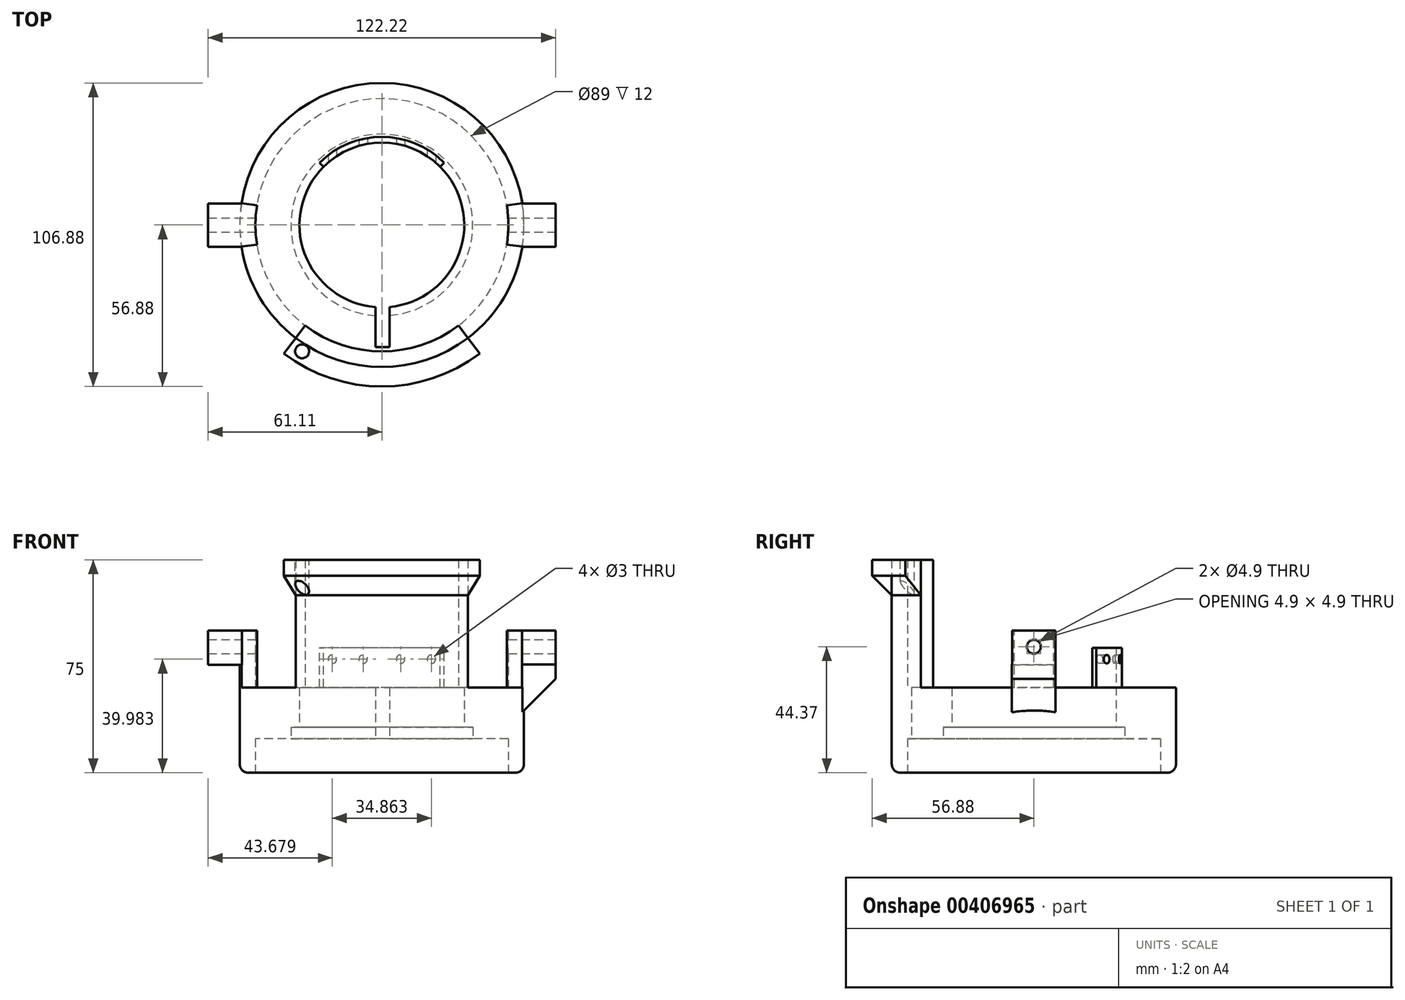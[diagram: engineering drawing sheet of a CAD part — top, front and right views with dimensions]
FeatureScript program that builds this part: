
annotation { "Feature Type Name" : "Feature", "Feature Type Description" : "" }
export const myFeature = defineFeature(function(context is Context, id is Id, definition is map)
    precondition{}
    {
        {
            var Q0;
            Q0=qCreatedBy(makeId("Top.planeOp"),FACE);
            var sketch = newSketch(context, id + "F0", { "sketchPlane" : qUnion([Q0])});
            skCircle(sketch, "E0", {"center": v(0, 0) * mm, "radius": 32 * mm});
            skCircle(sketch, "E1", {"center": v(0, 0) * mm, "radius": 44.5 * mm});
            skCircle(sketch, "E2", {"center": v(0, 0) * mm, "radius": 50 * mm});
            skCircle(sketch, "E3", {"center": v(0, 0) * mm, "radius": 29 * mm});
            skSolve(sketch);
        }
        {
            var Q0;
            Q0=makeQuery(id+"F0.imprint","IMPRINT",FACE,{"disambiguationData":[TD([[makeQuery(id+"F0.imprint","IMPRINT",EDGE,{"derivedFrom":sQuery(id+"F0.wireOp",EDGE,"E1")}),-1.0]])]});
            extrude(context, id + "F1", {"entities" : qUnion([Q0]), "depth" : 50 * mm});
        }
        {
            var Q0;
            Q0=makeQuery(id+"F0.imprint","IMPRINT",FACE,{"disambiguationData":[TD([[makeQuery(id+"F0.imprint","IMPRINT",EDGE,{"derivedFrom":sQuery(id+"F0.wireOp",EDGE,"E0")}),-1.0]])]});
            extrude(context, id + "F2", {"entities" : qUnion([Q0]), "operationType" : NewBodyOperationType.ADD, "depth" : 30 * mm, "hasSecondDirection" : true, "secondDirectionOppositeDirection" : false, "secondDirectionDepth" : 12 * mm});
        }
        {
            var Q0;
            Q0=makeQuery(id+"F0.imprint","IMPRINT",FACE,{"disambiguationData":[TD([[makeQuery(id+"F0.imprint","IMPRINT",EDGE,{"derivedFrom":sQuery(id+"F0.wireOp",EDGE,"E0")}),1.0]])]});
            extrude(context, id + "F3", {"entities" : qUnion([Q0]), "operationType" : NewBodyOperationType.ADD, "depth" : 30 * mm, "hasSecondDirection" : true, "secondDirectionOppositeDirection" : false, "secondDirectionDepth" : 16 * mm});
        }
        {
            var Q0;
            Q0=qCreatedBy(makeId("Top.planeOp"),FACE);
            var sketch = newSketch(context, id + "F4", { "sketchPlane" : qUnion([Q0])});
            skLineSegment(sketch, "E4.bottom", {"start": v(-2.3, -43.05) * mm, "end": v(2.7, -43.05) * mm});
            skLineSegment(sketch, "E4.top", {"start": v(-2.3, -28.05) * mm, "end": v(2.7, -28.05) * mm});
            skLineSegment(sketch, "E4.left", {"start": v(-2.3, -43.05) * mm, "end": v(-2.3, -28.05) * mm});
            skLineSegment(sketch, "E4.right", {"start": v(2.7, -43.05) * mm, "end": v(2.7, -28.05) * mm});
            skSolve(sketch);
        }
        {
            var Q0;
            Q0=makeQuery(id+"F4.imprint","IMPRINT",FACE,{"disambiguationData":[TD([[makeQuery(id+"F4.imprint","IMPRINT",EDGE,{"derivedFrom":sQuery(id+"F4.wireOp",EDGE,"E4.bottom")}),1.0]])]});
            var Q1;
            Q1=sQuery(id+"F4.wireOp",EDGE,"E4.right");
            var Q2;
            Q2=sQuery(id+"F4.wireOp",EDGE,"E4.top");
            var Q3;
            Q3=sQuery(id+"F4.wireOp",EDGE,"E4.left");
            var Q4;
            Q4=sQuery(id+"F4.wireOp",EDGE,"E4.bottom");
            extrude(context, id + "F5", {"entities" : qUnion([Q0]), "operationType" : NewBodyOperationType.REMOVE, "surfaceEntities" : qUnion([Q1, Q2, Q3, Q4]), "depth" : 35 * mm});
        }
        {
            var Q0;
            Q0=makeQuery(id+"F1.opExtrude","CAP_FACE",FACE,{"disambiguationData":[OSD([sQuery(id+"F0.wireOp",EDGE,"E1"),sQuery(id+"F0.wireOp",EDGE,"E2")])],"isStart":false});
            var sketch = newSketch(context, id + "F6", { "sketchPlane" : qUnion([Q0])});
            skLineSegment(sketch, "E5", {"start": v(30.3, -39.78) * mm, "end": v(26.96, -35.4) * mm});
            skLineSegment(sketch, "E6.MirrorCS", {"start": v(-30.3, -39.78) * mm, "end": v(-26.96, -35.4) * mm});
            skSolve(sketch);
        }
        {
            var Q0;
            Q0 = qSketchRegion(id + "F6", true);
            var Q1;
            {var subQ0=sQuery(id+"F6.wireOp",EDGE,"E5");Q1=makeQuery(id+"F6.imprint","IMPRINT",FACE,{"disambiguationData":[TD([[makeQuery(id+"F6.imprint","IMPRINT",EDGE,{"derivedFrom":subQ0}),1.0]])]});}
            extrude(context, id + "F7", {"entities" : qUnion([Q0, Q1]), "operationType" : NewBodyOperationType.ADD, "depth" : 25 * mm});
        }
        {
            var Q0;
            Q0=qCreatedBy(makeId("Right.planeOp"),FACE);
            var sketch = newSketch(context, id + "F8", { "sketchPlane" : qUnion([Q0])});
            skCircle(sketch, "E7", {"center": v(0, 44.37) * mm, "radius": 2.45 * mm});
            skSolve(sketch);
        }
        {
            var Q0;
            Q0=makeQuery(id+"F7.opExtrude","CAP_FACE",FACE,{"disambiguationData":[OSD([sQuery(id+"F0.wireOp",EDGE,"E1"),sQuery(id+"F0.wireOp",EDGE,"E2"),sQuery(id+"F6.wireOp",EDGE,"E5"),sQuery(id+"F6.wireOp",EDGE,"87c34836-5ebc-4285-9b58-168e83040a5a0.MirrorCS")])],"isStart":false});
            var sketch = newSketch(context, id + "F9", { "sketchPlane" : qUnion([Q0])});
            skCircle(sketch, "E8", {"center": v(-28.06, -44.5) * mm, "radius": 2.45 * mm});
            skCircle(sketch, "E9.MirrorC", {"center": v(28.06, -44.5) * mm, "radius": 2.45 * mm});
            skSolve(sketch);
        }
        {
            var Q0;
            Q0=qCreatedBy(makeId("Right.planeOp"),FACE);
            var sketch = newSketch(context, id + "F10", { "sketchPlane" : qUnion([Q0])});
            skLineSegment(sketch, "E10", {"start": v(0, 75.03) * mm, "end": v(0, -13.13) * mm});
            skSolve(sketch);
        }
        {
            var Q0;
            Q0=makeQuery(id+"F7.opExtrude","SWEPT_FACE",FACE,{"disambiguationData":[OSD([sQuery(id+"F6.wireOp",EDGE,"E5")])]});
            var sketch = newSketch(context, id + "F11", { "sketchPlane" : qUnion([Q0])});
            skLineSegment(sketch, "E11", {"start": v(-44.5, 75) * mm, "end": v(-56.88, 75) * mm});
            skLineSegment(sketch, "E12", {"start": v(-50, 62.5) * mm, "end": v(-50, 75) * mm});
            skLineSegment(sketch, "E13", {"start": v(-56.88, 75) * mm, "end": v(-56.88, 69.4) * mm});
            skLineSegment(sketch, "E14", {"start": v(-56.88, 69.4) * mm, "end": v(-50, 62.5) * mm});
            skSolve(sketch);
        }
        {
            var Q0;
            {var subQ0=sQuery(id+"F11.wireOp",EDGE,"E12");Q0=makeQuery(id+"F11.imprint","IMPRINT",FACE,{"disambiguationData":[TD([[makeQuery(id+"F11.imprint","IMPRINT",EDGE,{"derivedFrom":subQ0}),-1.0]])]});}
            var Q1;
            Q1=sQuery(id+"F10.wireOp",EDGE,"E10");
            revolve(context, id + "F12", {"entities" : qUnion([Q0]), "axis" : qUnion([Q1]), "revolveType" : RevolveType.ONE_DIRECTION, "angle" : 74.6 * degree});
        }
        {
            var Q0;
            Q0=makeQuery(id+"F9.imprint","IMPRINT",FACE,{"disambiguationData":[TD([[makeQuery(id+"F9.imprint","IMPRINT",EDGE,{"derivedFrom":sQuery(id+"F9.wireOp",EDGE,"E8")}),1.0]])]});
            var Q1;
            Q1=makeQuery(id+"F9.imprint","IMPRINT",FACE,{"disambiguationData":[TD([[makeQuery(id+"F9.imprint","IMPRINT",EDGE,{"derivedFrom":sQuery(id+"F9.wireOp",EDGE,"E9.MirrorC")}),-1.0]])]});
            extrude(context, id + "F13", {"entities" : qUnion([Q0, Q1]), "operationType" : NewBodyOperationType.REMOVE, "oppositeDirection" : true, "depth" : 25 * mm});
        }
        {
            var Q0;
            Q0=makeQuery(id+"F1.opExtrude","CAP_FACE",FACE,{"disambiguationData":[OSD([sQuery(id+"F0.wireOp",EDGE,"E1"),sQuery(id+"F0.wireOp",EDGE,"E2")])],"isStart":false});
            var sketch = newSketch(context, id + "F14", { "sketchPlane" : qUnion([Q0])});
            skLineSegment(sketch, "E15", {"start": v(49.42, -7.62) * mm, "end": v(43.96, -6.9) * mm});
            skLineSegment(sketch, "E16.MirrorCS", {"start": v(49.42, 7.62) * mm, "end": v(43.96, 6.9) * mm});
            skLineSegment(sketch, "E17.MirrorCS", {"start": v(-49.42, 7.62) * mm, "end": v(-43.96, 6.9) * mm});
            skLineSegment(sketch, "E18.MirrorCS", {"start": v(-49.42, -7.62) * mm, "end": v(-43.96, -6.9) * mm});
            skSolve(sketch);
        }
        {
            var Q0;
            {var subQ0=sQuery(id+"F14.wireOp",EDGE,"E15");Q0=makeQuery(id+"F14.imprint","IMPRINT",FACE,{"disambiguationData":[TD([[makeQuery(id+"F14.imprint","IMPRINT",EDGE,{"derivedFrom":subQ0}),1.0]])]});}
            var Q1;
            {var subQ0=sQuery(id+"F14.wireOp",EDGE,"E16.MirrorCS");Q1=makeQuery(id+"F14.imprint","IMPRINT",FACE,{"disambiguationData":[TD([[makeQuery(id+"F14.imprint","IMPRINT",EDGE,{"derivedFrom":subQ0}),-1.0]])]});}
            var Q2;
            {var subQ0=sQuery(id+"F14.wireOp",EDGE,"E18.MirrorCS");Q2=makeQuery(id+"F14.imprint","IMPRINT",FACE,{"disambiguationData":[TD([[makeQuery(id+"F14.imprint","IMPRINT",EDGE,{"derivedFrom":subQ0}),-1.0]])]});}
            extrude(context, id + "F15", {"entities" : qUnion([Q0, Q1, Q2]), "operationType" : NewBodyOperationType.REMOVE, "oppositeDirection" : true, "depth" : 20 * mm});
        }
        {
            var Q0;
            Q0=qCreatedBy(makeId("Top.planeOp"),FACE);
            var sketch = newSketch(context, id + "F16", { "sketchPlane" : qUnion([Q0])});
            skLineSegment(sketch, "E19.MirrorCS", {"start": v(-61.11, 7.6) * mm, "end": v(-49.36, 7.6) * mm});
            skLineSegment(sketch, "E20.MirrorCS", {"start": v(-49.3, -7.68) * mm, "end": v(-61.11, -7.68) * mm});
            skLineSegment(sketch, "E21.MirrorCS", {"start": v(-61.11, -7.68) * mm, "end": v(-61.11, 7.6) * mm});
            skArc(sketch, "E22", {"start": v(-49.36, 7.6) * mm, "mid": v(-49.86, -0.04) * mm, "end": v(-49.3, -7.68) * mm});
            skLineSegment(sketch, "E23.MirrorCS", {"start": v(61.11, 7.6) * mm, "end": v(49.36, 7.6) * mm});
            skLineSegment(sketch, "E24.MirrorCS", {"start": v(61.11, -7.68) * mm, "end": v(61.11, 7.6) * mm});
            skLineSegment(sketch, "E25.MirrorCS", {"start": v(49.3, -7.68) * mm, "end": v(61.11, -7.68) * mm});
            skArc(sketch, "E26.MirrorCS", {"start": v(49.36, 7.6) * mm, "mid": v(49.86, -0.04) * mm, "end": v(49.3, -7.68) * mm});
            skSolve(sketch);
        }
        {
            var Q0;
            Q0=makeQuery(id+"F16.imprint","IMPRINT",FACE,{"disambiguationData":[TD([[makeQuery(id+"F16.imprint","IMPRINT",EDGE,{"derivedFrom":sQuery(id+"F16.wireOp",EDGE,"E19.MirrorCS")}),-1.0]])]});
            var Q1;
            Q1=makeQuery(id+"F16.imprint","IMPRINT",FACE,{"disambiguationData":[TD([[makeQuery(id+"F16.imprint","IMPRINT",EDGE,{"derivedFrom":sQuery(id+"F16.wireOp",EDGE,"E23.MirrorCS")}),1.0]])]});
            extrude(context, id + "F17", {"entities" : qUnion([Q0, Q1]), "operationType" : NewBodyOperationType.ADD, "depth" : 50 * mm, "hasSecondDirection" : true, "secondDirectionOppositeDirection" : false, "secondDirectionDepth" : 38 * mm});
        }
        {
            var Q0;
            Q0=qCreatedBy(makeId("Top.planeOp"),FACE);
            var sketch = newSketch(context, id + "F18", { "sketchPlane" : qUnion([Q0])});
            skLineSegment(sketch, "E27", {"start": v(49.36, -7.71) * mm, "end": v(61.1, -7.71) * mm});
            skLineSegment(sketch, "E28", {"start": v(61.1, -7.71) * mm, "end": v(61.1, 7.58) * mm});
            skLineSegment(sketch, "E29", {"start": v(61.1, 7.58) * mm, "end": v(49.42, 7.58) * mm});
            skArc(sketch, "E30", {"start": v(49.36, -7.71) * mm, "mid": v(49.84, -0.07) * mm, "end": v(49.42, 7.58) * mm});
            skArc(sketch, "E31.MirrorCS", {"start": v(-49.36, -7.71) * mm, "mid": v(-49.84, -0.07) * mm, "end": v(-49.42, 7.58) * mm});
            skLineSegment(sketch, "E32.MirrorCS", {"start": v(-49.36, -7.71) * mm, "end": v(-61.1, -7.71) * mm});
            skLineSegment(sketch, "E33.MirrorCS", {"start": v(-61.1, -7.71) * mm, "end": v(-61.1, 7.58) * mm});
            skLineSegment(sketch, "E34.MirrorCS", {"start": v(-61.1, 7.58) * mm, "end": v(-49.42, 7.58) * mm});
            skSolve(sketch);
        }
        {
            var Q0;
            Q0=makeQuery(id+"F18.imprint","IMPRINT",FACE,{"disambiguationData":[TD([[makeQuery(id+"F18.imprint","IMPRINT",EDGE,{"derivedFrom":sQuery(id+"F18.wireOp",EDGE,"E27")}),1.0]])]});
            var Q1;
            Q1=makeQuery(id+"F18.imprint","IMPRINT",FACE,{"disambiguationData":[TD([[makeQuery(id+"F18.imprint","IMPRINT",EDGE,{"derivedFrom":sQuery(id+"F18.wireOp",EDGE,"E31.MirrorCS")}),1.0]])]});
            extrude(context, id + "F19", {"entities" : qUnion([Q0, Q1]), "operationType" : NewBodyOperationType.ADD, "depth" : 38.1 * mm, "hasSecondDirection" : true, "secondDirectionOppositeDirection" : false, "secondDirectionDepth" : 20 * mm});
        }
        {
            var Q0;
            Q0=makeQuery(id+"F19.opExtrude","CAP_EDGE",EDGE,{"disambiguationData":[OSD([sQuery(id+"F18.wireOp",EDGE,"E33.MirrorCS")])],"isStart":true});
            var Q1;
            Q1=makeQuery(id+"F19.opExtrude","CAP_EDGE",EDGE,{"disambiguationData":[OSD([sQuery(id+"F18.wireOp",EDGE,"E28")])],"isStart":true});
            chamfer(context, id + "F20", {"entities" : qUnion([Q0, Q1]), "width" : 13 * mm, "tangentPropagation" : true});
        }
        {
            var Q0;
            Q0 = qSketchRegion(id + "F8", true);
            extrude(context, id + "F21", {"entities" : qUnion([Q0]), "operationType" : NewBodyOperationType.REMOVE, "oppositeDirection" : true, "depth" : 77.7 * mm, "hasSecondDirection" : true, "secondDirectionOppositeDirection" : false, "secondDirectionDepth" : 72.9 * mm});
        }
        {
            var Q0;
            Q0=makeQuery(id+"F1.opExtrude","CAP_EDGE",EDGE,{"disambiguationData":[OSD([sQuery(id+"F0.wireOp",EDGE,"E2")])],"isStart":true});
            fillet(context, id + "F22", {"entities" : qUnion([Q0]), "radius" : 3 * mm, "tangentPropagation" : true, "allowEdgeOverflow" : false});
        }
        {
            var Q0;
            {var subQ0=sQuery(id+"F0.wireOp",EDGE,"E2");var subQ1=sQuery(id+"F0.wireOp",EDGE,"E1");var subQ2=sQuery(id+"F0.wireOp",EDGE,"E0");Q0=makeQuery(id+"F15.boolean.opBoolean","MERGE",FACE,{"derivedFrom":[makeQuery(id+"F3.boolean.opBoolean","MERGE",FACE,{"derivedFrom":[makeQuery(id+"F2.opExtrude","CAP_FACE",FACE,{"disambiguationData":[OSD([subQ2,subQ1])],"isStart":false}),makeQuery(id+"F3.opExtrude","CAP_FACE",FACE,{"disambiguationData":[OSD([subQ2,sQuery(id+"F0.wireOp",EDGE,"E3")])],"isStart":false})]}),makeQuery(id+"F15.opExtrude","CAP_FACE",FACE,{"disambiguationData":[OSD([subQ1,subQ0,sQuery(id+"F6.wireOp",EDGE,"E5"),sQuery(id+"F14.wireOp",EDGE,"E15")])],"isStart":false}),makeQuery(id+"F15.opExtrude","CAP_FACE",FACE,{"disambiguationData":[OSD([subQ1,subQ0,sQuery(id+"F14.wireOp",EDGE,"E16.MirrorCS"),sQuery(id+"F14.wireOp",EDGE,"E17.MirrorCS")])],"isStart":false}),makeQuery(id+"F15.opExtrude","CAP_FACE",FACE,{"disambiguationData":[OSD([subQ1,subQ0,sQuery(id+"F6.wireOp",EDGE,"E6.MirrorCS"),sQuery(id+"F14.wireOp",EDGE,"E18.MirrorCS")])],"isStart":false})]});}
            var sketch = newSketch(context, id + "F23", { "sketchPlane" : qUnion([Q0])});
            skCircle(sketch, "E35.0", {"center": v(0, 0) * mm, "radius": 31 * mm});
            skSolve(sketch);
        }
        {
            var Q0;
            {var subQ1=sQuery(id+"F0.wireOp",EDGE,"E3");var subQ8=makeQuery(id+"F3.opExtrude","CAP_EDGE",EDGE,{"disambiguationData":[OSD([subQ1])],"isStart":false});Q0=makeQuery(id+"F23.imprint","IMPRINT",FACE,{"disambiguationData":[TD([[makeQuery(id+"F23.imprint","IMPRINT",EDGE,{"derivedFrom":subQ8}),-1.0]])]});}
            extrude(context, id + "F24", {"entities" : qUnion([Q0]), "operationType" : NewBodyOperationType.ADD, "depth" : 14 * mm});
        }
        {
            var Q0;
            Q0=makeQuery(id+"F24.opExtrude","CAP_FACE",FACE,{"disambiguationData":[OSD([sQuery(id+"F0.wireOp",EDGE,"E0"),sQuery(id+"F0.wireOp",EDGE,"E1"),sQuery(id+"F0.wireOp",EDGE,"E3"),sQuery(id+"F4.wireOp",EDGE,"E4.left"),sQuery(id+"F4.wireOp",EDGE,"E4.right"),sQuery(id+"F23.wireOp",EDGE,"E35.0")])],"isStart":false});
            var sketch = newSketch(context, id + "F25", { "sketchPlane" : qUnion([Q0])});
            skLineSegment(sketch, "E36", {"start": v(-75, 75) * mm, "end": v(75, -75) * mm});
            skLineSegment(sketch, "E37.MirrorCS", {"start": v(75, 75) * mm, "end": v(-75, -75) * mm});
            skSolve(sketch);
        }
        {
            var Q0;
            {var subQ0=sQuery(id+"F25.wireOp",EDGE,"E36");var subQ1=makeQuery(id+"F24.opExtrude","CAP_EDGE",EDGE,{"disambiguationData":[OSD([sQuery(id+"F23.wireOp",EDGE,"E35.0")])],"isStart":false});var subQ2=makeQuery(id+"F25.imprint","INTERSECT",VERTEX,{"disambiguationData":[OD(0.0)],"derivedFrom":[subQ1,subQ0]});Q0=makeQuery(id+"F25.imprint","IMPRINT",FACE,{"disambiguationData":[TD([[makeQuery(id+"F25.imprint","IMPRINT",EDGE,{"disambiguationData":[TD([[subQ2,-1.0]])],"derivedFrom":subQ0}),-1.0]])]});}
            var Q1;
            {var subQ0=sQuery(id+"F25.wireOp",EDGE,"E36");var subQ1=makeQuery(id+"F24.opExtrude","CAP_EDGE",EDGE,{"disambiguationData":[OSD([sQuery(id+"F23.wireOp",EDGE,"E35.0")])],"isStart":false});var subQ2=makeQuery(id+"F25.imprint","INTERSECT",VERTEX,{"disambiguationData":[OD(1.0)],"derivedFrom":[subQ1,subQ0]});Q1=makeQuery(id+"F25.imprint","IMPRINT",FACE,{"disambiguationData":[TD([[makeQuery(id+"F25.imprint","IMPRINT",EDGE,{"disambiguationData":[TD([[subQ2,1.0]])],"derivedFrom":subQ0}),1.0]])]});}
            var Q2;
            {var subQ3=sQuery(id+"F0.wireOp",EDGE,"E3");var subQ6=makeQuery(id+"F24.opExtrude","CAP_EDGE",EDGE,{"disambiguationData":[OSD([sQuery(id+"F0.wireOp",EDGE,"E0"),sQuery(id+"F0.wireOp",EDGE,"E1"),subQ3,sQuery(id+"F4.wireOp",EDGE,"E4.right")])],"isStart":false});Q2=makeQuery(id+"F25.imprint","IMPRINT",FACE,{"disambiguationData":[TD([[makeQuery(id+"F25.imprint","IMPRINT",EDGE,{"derivedFrom":subQ6}),1.0]])]});}
            var Q3;
            {var subQ3=sQuery(id+"F0.wireOp",EDGE,"E3");var subQ6=makeQuery(id+"F24.opExtrude","CAP_EDGE",EDGE,{"disambiguationData":[OSD([sQuery(id+"F0.wireOp",EDGE,"E0"),sQuery(id+"F0.wireOp",EDGE,"E1"),subQ3,sQuery(id+"F4.wireOp",EDGE,"E4.left")])],"isStart":false});Q3=makeQuery(id+"F25.imprint","IMPRINT",FACE,{"disambiguationData":[TD([[makeQuery(id+"F25.imprint","IMPRINT",EDGE,{"derivedFrom":subQ6}),-1.0]])]});}
            extrude(context, id + "F26", {"entities" : qUnion([Q0, Q1, Q2, Q3]), "operationType" : NewBodyOperationType.REMOVE, "oppositeDirection" : true, "depth" : 14 * mm});
        }
        {
            var Q0;
            Q0=qCreatedBy(makeId("Front.planeOp"),FACE);
            var sketch = newSketch(context, id + "F27", { "sketchPlane" : qUnion([Q0])});
            skCircle(sketch, "E38", {"center": v(17.43, 39.98) * mm, "radius": 1.5 * mm});
            skCircle(sketch, "E39", {"center": v(6.6, 39.98) * mm, "radius": 1.5 * mm});
            skCircle(sketch, "E40.MirrorC", {"center": v(-6.6, 39.98) * mm, "radius": 1.5 * mm});
            skCircle(sketch, "E41.MirrorC", {"center": v(-17.43, 39.98) * mm, "radius": 1.5 * mm});
            skSolve(sketch);
        }
        {
            var Q0;
            Q0 = qSketchRegion(id + "F27", true);
            extrude(context, id + "F28", {"entities" : qUnion([Q0]), "operationType" : NewBodyOperationType.REMOVE, "oppositeDirection" : true, "depth" : 37 * mm});
        }
    });
